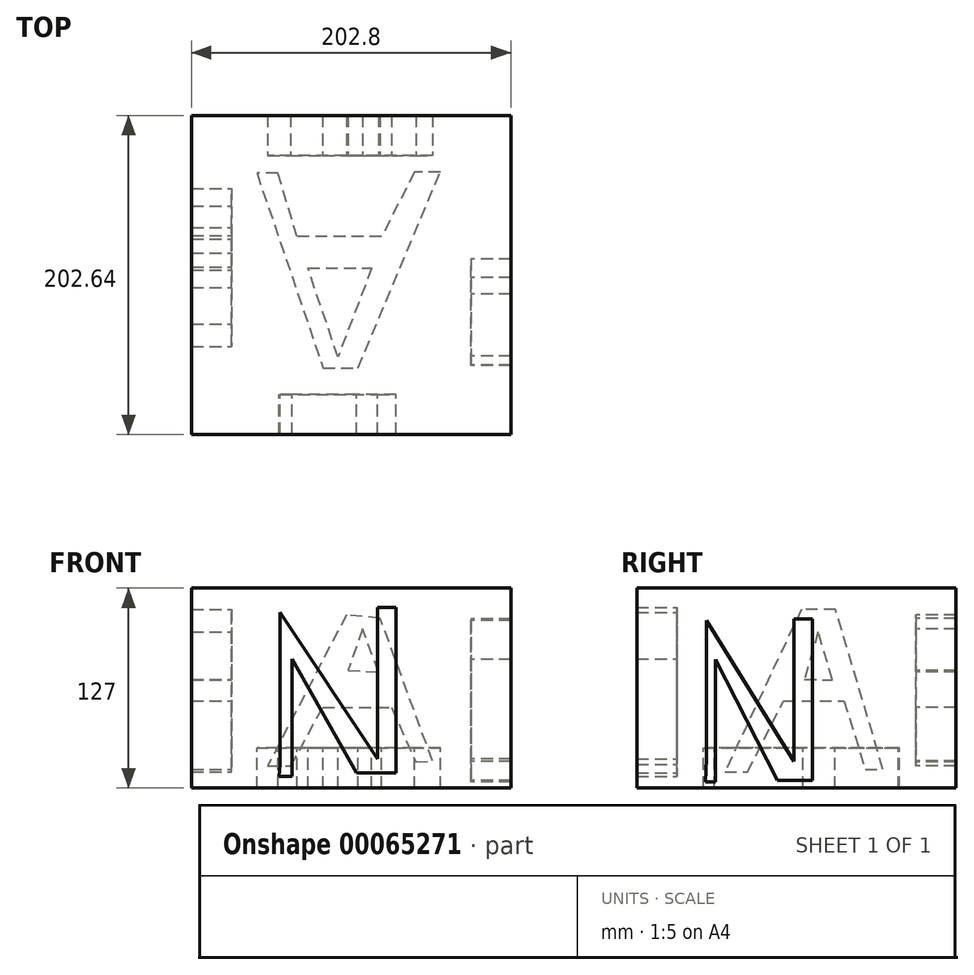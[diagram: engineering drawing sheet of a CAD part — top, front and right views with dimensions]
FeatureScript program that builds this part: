
annotation { "Feature Type Name" : "Feature", "Feature Type Description" : "" }
export const myFeature = defineFeature(function(context is Context, id is Id, definition is map)
    precondition{}
    {
        {
            var Q0;
            Q0=qCreatedBy(makeId("Top.planeOp"),FACE);
            var sketch = newSketch(context, id + "F0", { "sketchPlane" : qUnion([Q0])});
            skLineSegment(sketch, "E0.bottom", {"start": v(-76, 76.16) * mm, "end": v(76, 76.16) * mm});
            skLineSegment(sketch, "E0.top", {"start": v(-76, -75.68) * mm, "end": v(76, -75.68) * mm});
            skLineSegment(sketch, "E0.left", {"start": v(-76, 76.16) * mm, "end": v(-76, -75.68) * mm});
            skLineSegment(sketch, "E0.right", {"start": v(76, 76.16) * mm, "end": v(76, -75.68) * mm});
            skSolve(sketch);
        }
        {
            var Q0;
            Q0=makeQuery(id+"F0.imprint","IMPRINT",FACE,{"disambiguationData":[TD([[makeQuery(id+"F0.imprint","IMPRINT",EDGE,{"derivedFrom":sQuery(id+"F0.wireOp",EDGE,"E0.bottom")}),-1.0]])]});
            extrude(context, id + "F1", {"entities" : qUnion([Q0]), "depth" : 25.4 * mm});
        }
        {
            var Q0;
            Q0=makeQuery(id+"F1.opExtrude","CAP_FACE",FACE,{"disambiguationData":[OSD([sQuery(id+"F0.wireOp",EDGE,"E0.bottom"),sQuery(id+"F0.wireOp",EDGE,"E0.top"),sQuery(id+"F0.wireOp",EDGE,"E0.left"),sQuery(id+"F0.wireOp",EDGE,"E0.right")])],"isStart":false});
            extrude(context, id + "F2", {"entities" : qUnion([Q0]), "operationType" : NewBodyOperationType.ADD, "depth" : 25.4 * mm});
        }
        {
            var Q0;
            Q0=makeQuery(id+"F2.opExtrude","CAP_FACE",FACE,{"disambiguationData":[OSD([sQuery(id+"F0.wireOp",EDGE,"E0.bottom"),sQuery(id+"F0.wireOp",EDGE,"E0.top"),sQuery(id+"F0.wireOp",EDGE,"E0.left"),sQuery(id+"F0.wireOp",EDGE,"E0.right")])],"isStart":false});
            var sketch = newSketch(context, id + "F3", { "sketchPlane" : qUnion([Q0])});
            skLineSegment(sketch, "E1", {"start": v(-54.36, -51.73) * mm, "end": v(-54.36, 43.28) * mm});
            skLineSegment(sketch, "E2", {"start": v(-54.36, 43.28) * mm, "end": v(20.97, -43.16) * mm});
            skLineSegment(sketch, "E3", {"start": v(20.97, -43.16) * mm, "end": v(29.1, -51.72) * mm});
            skLineSegment(sketch, "E4", {"start": v(29.1, -51.72) * mm, "end": v(30.75, 43.95) * mm});
            skLineSegment(sketch, "E5", {"start": v(30.75, 43.95) * mm, "end": v(45.75, 43.7) * mm});
            skLineSegment(sketch, "E6", {"start": v(45.75, 43.7) * mm, "end": v(45.75, -59.02) * mm});
            skLineSegment(sketch, "E7", {"start": v(45.75, -59.02) * mm, "end": v(20.4, -59.02) * mm});
            skLineSegment(sketch, "E8", {"start": v(20.4, -59.02) * mm, "end": v(-46.22, 21.24) * mm});
            skLineSegment(sketch, "E9", {"start": v(-46.22, 21.24) * mm, "end": v(-46.22, -60.24) * mm});
            skLineSegment(sketch, "E10", {"start": v(-46.22, -60.24) * mm, "end": v(-54.78, -60.24) * mm});
            skLineSegment(sketch, "E11", {"start": v(-54.78, -60.24) * mm, "end": v(-54.36, -51.73) * mm});
            skSolve(sketch);
        }
        {
            var Q0;
            Q0=makeQuery(id+"F3.imprint","IMPRINT",FACE,{"disambiguationData":[TD([[makeQuery(id+"F3.imprint","IMPRINT",EDGE,{"derivedFrom":sQuery(id+"F3.wireOp",EDGE,"E1")}),1.0]])]});
            extrude(context, id + "F4", {"entities" : qUnion([Q0]), "operationType" : NewBodyOperationType.ADD, "depth" : 25.4 * mm});
        }
        {
            var Q0;
            Q0=makeQuery(id+"F1.opExtrude","CAP_FACE",FACE,{"disambiguationData":[OSD([sQuery(id+"F0.wireOp",EDGE,"E0.bottom"),sQuery(id+"F0.wireOp",EDGE,"E0.top"),sQuery(id+"F0.wireOp",EDGE,"E0.left"),sQuery(id+"F0.wireOp",EDGE,"E0.right")])],"isStart":true});
            extrude(context, id + "F5", {"entities" : qUnion([Q0]), "operationType" : NewBodyOperationType.ADD, "depth" : 25.4 * mm});
        }
        {
            var Q0;
            Q0=makeQuery(id+"F5.opExtrude","CAP_FACE",FACE,{"disambiguationData":[OSD([sQuery(id+"F0.wireOp",EDGE,"E0.bottom"),sQuery(id+"F0.wireOp",EDGE,"E0.top"),sQuery(id+"F0.wireOp",EDGE,"E0.left"),sQuery(id+"F0.wireOp",EDGE,"E0.right")])],"isStart":false});
            var sketch = newSketch(context, id + "F6", { "sketchPlane" : qUnion([Q0])});
            skLineSegment(sketch, "E12", {"start": v(-59.88, -64.92) * mm, "end": v(-17.83, 58.84) * mm});
            skLineSegment(sketch, "E13", {"start": v(-17.83, 58.84) * mm, "end": v(4.24, 58.84) * mm});
            skLineSegment(sketch, "E14", {"start": v(4.24, 58.84) * mm, "end": v(56.69, -65.72) * mm});
            skLineSegment(sketch, "E15", {"start": v(56.69, -65.72) * mm, "end": v(40.22, -65.72) * mm});
            skLineSegment(sketch, "E16", {"start": v(40.22, -65.72) * mm, "end": v(19.27, -24.63) * mm});
            skLineSegment(sketch, "E17", {"start": v(19.27, -24.63) * mm, "end": v(-34.3, -24.63) * mm});
            skLineSegment(sketch, "E18", {"start": v(-34.3, -24.63) * mm, "end": v(-46.61, -64.92) * mm});
            skLineSegment(sketch, "E19", {"start": v(-46.61, -64.92) * mm, "end": v(-59.88, -64.92) * mm});
            skLineSegment(sketch, "E20", {"start": v(-8.71, 45.41) * mm, "end": v(-28.7, -13.38) * mm});
            skLineSegment(sketch, "E21", {"start": v(-28.7, -13.38) * mm, "end": v(15.91, -13.38) * mm});
            skLineSegment(sketch, "E22", {"start": v(15.91, -13.38) * mm, "end": v(-8.71, 45.41) * mm});
            skSolve(sketch);
        }
        {
            var Q0;
            Q0=makeQuery(id+"F6.imprint","IMPRINT",FACE,{"disambiguationData":[TD([[makeQuery(id+"F6.imprint","IMPRINT",EDGE,{"derivedFrom":sQuery(id+"F6.wireOp",EDGE,"E12")}),1.0]])]});
            extrude(context, id + "F7", {"entities" : qUnion([Q0]), "operationType" : NewBodyOperationType.ADD, "depth" : 25.4 * mm});
        }
        {
            var Q0;
            Q0=makeQuery(id+"F5.opExtrude","CAP_FACE",FACE,{"disambiguationData":[OSD([sQuery(id+"F0.wireOp",EDGE,"E0.bottom"),sQuery(id+"F0.wireOp",EDGE,"E0.top"),sQuery(id+"F0.wireOp",EDGE,"E0.left"),sQuery(id+"F0.wireOp",EDGE,"E0.right")])],"isStart":false});
            var sketch = newSketch(context, id + "F8", { "sketchPlane" : qUnion([Q0])});
            skLineSegment(sketch, "E23", {"start": v(-8.4, 51.8) * mm, "end": v(-27.54, -4.55) * mm});
            skLineSegment(sketch, "E24", {"start": v(-27.54, -4.55) * mm, "end": v(13.03, -4.55) * mm});
            skLineSegment(sketch, "E25", {"start": v(13.03, -4.55) * mm, "end": v(-8.4, 51.8) * mm});
            skSolve(sketch);
        }
        {
            var Q0;
            Q0=makeQuery(id+"F8.imprint","IMPRINT",FACE,{"disambiguationData":[TD([[makeQuery(id+"F8.imprint","IMPRINT",EDGE,{"derivedFrom":sQuery(id+"F8.wireOp",EDGE,"E23")}),1.0]])]});
            extrude(context, id + "F9", {"entities" : qUnion([Q0]), "operationType" : NewBodyOperationType.ADD, "depth" : 25.4 * mm});
        }
        {
            var Q0;
            {var subQ0=sQuery(id+"F0.wireOp",EDGE,"E0.top");Q0=makeQuery(id+"F7.boolean.opBoolean","MERGE",FACE,{"derivedFrom":[makeQuery(id+"F5.boolean.opBoolean","MERGE",FACE,{"derivedFrom":[makeQuery(id+"F4.boolean.opBoolean","MERGE",FACE,{"derivedFrom":[makeQuery(id+"F2.boolean.opBoolean","MERGE",FACE,{"derivedFrom":[makeQuery(id+"F1.opExtrude","SWEPT_FACE",FACE,{"disambiguationData":[OSD([subQ0])]}),makeQuery(id+"F2.opExtrude","SWEPT_FACE",FACE,{"disambiguationData":[OSD([subQ0])]})]}),makeQuery(id+"F4.opExtrude","SWEPT_FACE",FACE,{"disambiguationData":[OSD([subQ0])]})]}),makeQuery(id+"F5.opExtrude","SWEPT_FACE",FACE,{"disambiguationData":[OSD([subQ0])]})]}),makeQuery(id+"F7.opExtrude","SWEPT_FACE",FACE,{"disambiguationData":[OSD([subQ0])]})]});}
            var sketch = newSketch(context, id + "F10", { "sketchPlane" : qUnion([Q0])});
            skLineSegment(sketch, "E26", {"start": v(-45.26, -35.73) * mm, "end": v(-45.26, 60.85) * mm});
            skLineSegment(sketch, "E27", {"start": v(-45.26, 60.85) * mm, "end": v(16.72, -32.28) * mm});
            skLineSegment(sketch, "E28", {"start": v(16.72, -32.28) * mm, "end": v(16.72, 63.93) * mm});
            skLineSegment(sketch, "E29", {"start": v(16.72, 63.93) * mm, "end": v(28.37, 63.93) * mm});
            skLineSegment(sketch, "E30", {"start": v(28.37, 63.93) * mm, "end": v(28.37, -41.2) * mm});
            skLineSegment(sketch, "E31", {"start": v(28.37, -41.2) * mm, "end": v(3.29, -41.2) * mm});
            skLineSegment(sketch, "E32", {"start": v(3.29, -41.2) * mm, "end": v(-37.55, 31.05) * mm});
            skLineSegment(sketch, "E33", {"start": v(-37.55, 31.05) * mm, "end": v(-37.55, -43.29) * mm});
            skLineSegment(sketch, "E34", {"start": v(-37.55, -43.29) * mm, "end": v(-45.73, -43.29) * mm});
            skLineSegment(sketch, "E35", {"start": v(-45.73, -43.29) * mm, "end": v(-45.26, -35.73) * mm});
            skSolve(sketch);
        }
        {
            var Q0;
            Q0=makeQuery(id+"F10.imprint","IMPRINT",FACE,{"disambiguationData":[TD([[makeQuery(id+"F10.imprint","IMPRINT",EDGE,{"derivedFrom":sQuery(id+"F10.wireOp",EDGE,"E26")}),1.0]])]});
            extrude(context, id + "F11", {"entities" : qUnion([Q0]), "operationType" : NewBodyOperationType.ADD, "depth" : 25.4 * mm});
        }
        {
            var Q0;
            {var subQ0=sQuery(id+"F0.wireOp",EDGE,"E0.bottom");Q0=makeQuery(id+"F7.boolean.opBoolean","MERGE",FACE,{"derivedFrom":[makeQuery(id+"F5.boolean.opBoolean","MERGE",FACE,{"derivedFrom":[makeQuery(id+"F4.boolean.opBoolean","MERGE",FACE,{"derivedFrom":[makeQuery(id+"F2.boolean.opBoolean","MERGE",FACE,{"derivedFrom":[makeQuery(id+"F1.opExtrude","SWEPT_FACE",FACE,{"disambiguationData":[OSD([subQ0])]}),makeQuery(id+"F2.opExtrude","SWEPT_FACE",FACE,{"disambiguationData":[OSD([subQ0])]})]}),makeQuery(id+"F4.opExtrude","SWEPT_FACE",FACE,{"disambiguationData":[OSD([subQ0])]})]}),makeQuery(id+"F5.opExtrude","SWEPT_FACE",FACE,{"disambiguationData":[OSD([subQ0])]})]}),makeQuery(id+"F7.opExtrude","SWEPT_FACE",FACE,{"disambiguationData":[OSD([subQ0])]})]});}
            var sketch = newSketch(context, id + "F12", { "sketchPlane" : qUnion([Q0])});
            skLineSegment(sketch, "E36", {"start": v(-51.68, -33.73) * mm, "end": v(-18.36, 56.94) * mm});
            skLineSegment(sketch, "E37", {"start": v(-18.36, 56.94) * mm, "end": v(3.06, 59.07) * mm});
            skLineSegment(sketch, "E38", {"start": v(3.06, 59.07) * mm, "end": v(53.14, -36.86) * mm});
            skLineSegment(sketch, "E39", {"start": v(53.14, -36.86) * mm, "end": v(38.44, -36.86) * mm});
            skLineSegment(sketch, "E40", {"start": v(38.44, -36.86) * mm, "end": v(18.05, 0.39) * mm});
            skLineSegment(sketch, "E41", {"start": v(18.05, 0.39) * mm, "end": v(-25.55, 0.39) * mm});
            skLineSegment(sketch, "E42", {"start": v(-25.55, 0.39) * mm, "end": v(-41, -34.15) * mm});
            skLineSegment(sketch, "E43", {"start": v(-41, -34.15) * mm, "end": v(-51.68, -33.73) * mm});
            skSolve(sketch);
        }
        {
            var Q0;
            Q0=makeQuery(id+"F12.imprint","IMPRINT",FACE,{"disambiguationData":[TD([[makeQuery(id+"F12.imprint","IMPRINT",EDGE,{"derivedFrom":sQuery(id+"F12.wireOp",EDGE,"E36")}),1.0]])]});
            extrude(context, id + "F13", {"entities" : qUnion([Q0]), "operationType" : NewBodyOperationType.ADD, "depth" : 25.4 * mm});
        }
        {
            var Q0;
            {var subQ0=sQuery(id+"F0.wireOp",EDGE,"E0.bottom");Q0=makeQuery(id+"F7.boolean.opBoolean","MERGE",FACE,{"derivedFrom":[makeQuery(id+"F5.boolean.opBoolean","MERGE",FACE,{"derivedFrom":[makeQuery(id+"F4.boolean.opBoolean","MERGE",FACE,{"derivedFrom":[makeQuery(id+"F2.boolean.opBoolean","MERGE",FACE,{"derivedFrom":[makeQuery(id+"F1.opExtrude","SWEPT_FACE",FACE,{"disambiguationData":[OSD([subQ0])]}),makeQuery(id+"F2.opExtrude","SWEPT_FACE",FACE,{"disambiguationData":[OSD([subQ0])]})]}),makeQuery(id+"F4.opExtrude","SWEPT_FACE",FACE,{"disambiguationData":[OSD([subQ0])]})]}),makeQuery(id+"F5.opExtrude","SWEPT_FACE",FACE,{"disambiguationData":[OSD([subQ0])]})]}),makeQuery(id+"F7.opExtrude","SWEPT_FACE",FACE,{"disambiguationData":[OSD([subQ0])]})]});}
            var sketch = newSketch(context, id + "F14", { "sketchPlane" : qUnion([Q0])});
            skLineSegment(sketch, "E44", {"start": v(-17.26, 22.94) * mm, "end": v(-7.29, 50.07) * mm});
            skLineSegment(sketch, "E45", {"start": v(-7.29, 50.07) * mm, "end": v(1.96, 23.8) * mm});
            skLineSegment(sketch, "E46", {"start": v(1.96, 23.8) * mm, "end": v(-17.26, 22.94) * mm});
            skSolve(sketch);
        }
        {
            var Q0;
            Q0=makeQuery(id+"F14.imprint","IMPRINT",FACE,{"disambiguationData":[TD([[makeQuery(id+"F14.imprint","IMPRINT",EDGE,{"derivedFrom":sQuery(id+"F14.wireOp",EDGE,"E44")}),-1.0]])]});
            extrude(context, id + "F15", {"entities" : qUnion([Q0]), "operationType" : NewBodyOperationType.ADD, "depth" : 25.4 * mm});
        }
        {
            var Q0;
            {var subQ0=sQuery(id+"F0.wireOp",EDGE,"E0.right");Q0=makeQuery(id+"F13.boolean.opBoolean","MERGE",FACE,{"derivedFrom":[makeQuery(id+"F11.boolean.opBoolean","MERGE",FACE,{"derivedFrom":[makeQuery(id+"F7.boolean.opBoolean","MERGE",FACE,{"derivedFrom":[makeQuery(id+"F5.boolean.opBoolean","MERGE",FACE,{"derivedFrom":[makeQuery(id+"F4.boolean.opBoolean","MERGE",FACE,{"derivedFrom":[makeQuery(id+"F2.boolean.opBoolean","MERGE",FACE,{"derivedFrom":[makeQuery(id+"F1.opExtrude","SWEPT_FACE",FACE,{"disambiguationData":[OSD([subQ0])]}),makeQuery(id+"F2.opExtrude","SWEPT_FACE",FACE,{"disambiguationData":[OSD([subQ0])]})]}),makeQuery(id+"F4.opExtrude","SWEPT_FACE",FACE,{"disambiguationData":[OSD([subQ0])]})]}),makeQuery(id+"F5.opExtrude","SWEPT_FACE",FACE,{"disambiguationData":[OSD([subQ0])]})]}),makeQuery(id+"F7.opExtrude","SWEPT_FACE",FACE,{"disambiguationData":[OSD([subQ0])]})]}),makeQuery(id+"F11.opExtrude","SWEPT_FACE",FACE,{"disambiguationData":[OSD([sQuery(id+"F0.wireOp",EDGE,"E0.top"),subQ0])]})]}),makeQuery(id+"F13.opExtrude","SWEPT_FACE",FACE,{"disambiguationData":[OSD([sQuery(id+"F0.wireOp",EDGE,"E0.bottom"),subQ0])]})]});}
            var sketch = newSketch(context, id + "F16", { "sketchPlane" : qUnion([Q0])});
            skLineSegment(sketch, "E47", {"start": v(-56.8, -32.44) * mm, "end": v(-56.8, 55.57) * mm});
            skLineSegment(sketch, "E48", {"start": v(-56.8, 55.57) * mm, "end": v(-1.43, -33.78) * mm});
            skLineSegment(sketch, "E49", {"start": v(-1.43, -33.78) * mm, "end": v(-1.43, 56.64) * mm});
            skLineSegment(sketch, "E50", {"start": v(-1.43, 56.64) * mm, "end": v(10.47, 56.64) * mm});
            skLineSegment(sketch, "E51", {"start": v(10.47, 56.64) * mm, "end": v(10.47, 55.97) * mm});
            skLineSegment(sketch, "E52", {"start": v(10.47, 55.97) * mm, "end": v(10.47, -45.82) * mm});
            skLineSegment(sketch, "E53", {"start": v(10.47, -45.82) * mm, "end": v(-11.86, -45.82) * mm});
            skLineSegment(sketch, "E54", {"start": v(-11.86, -45.82) * mm, "end": v(-51.05, 30.82) * mm});
            skLineSegment(sketch, "E55", {"start": v(-51.05, 30.82) * mm, "end": v(-51.05, -46.89) * mm});
            skLineSegment(sketch, "E56", {"start": v(-51.05, -46.89) * mm, "end": v(-57.34, -46.89) * mm});
            skLineSegment(sketch, "E57", {"start": v(-57.34, -46.89) * mm, "end": v(-56.8, -32.44) * mm});
            skSolve(sketch);
        }
        {
            var Q0;
            Q0=makeQuery(id+"F16.imprint","IMPRINT",FACE,{"disambiguationData":[TD([[makeQuery(id+"F16.imprint","IMPRINT",EDGE,{"derivedFrom":sQuery(id+"F16.wireOp",EDGE,"E47")}),1.0]])]});
            extrude(context, id + "F17", {"entities" : qUnion([Q0]), "operationType" : NewBodyOperationType.ADD, "depth" : 25.4 * mm});
        }
        {
            var Q0;
            {var subQ0=sQuery(id+"F0.wireOp",EDGE,"E0.left");Q0=makeQuery(id+"F13.boolean.opBoolean","MERGE",FACE,{"derivedFrom":[makeQuery(id+"F11.boolean.opBoolean","MERGE",FACE,{"derivedFrom":[makeQuery(id+"F7.boolean.opBoolean","MERGE",FACE,{"derivedFrom":[makeQuery(id+"F5.boolean.opBoolean","MERGE",FACE,{"derivedFrom":[makeQuery(id+"F4.boolean.opBoolean","MERGE",FACE,{"derivedFrom":[makeQuery(id+"F2.boolean.opBoolean","MERGE",FACE,{"derivedFrom":[makeQuery(id+"F1.opExtrude","SWEPT_FACE",FACE,{"disambiguationData":[OSD([subQ0])]}),makeQuery(id+"F2.opExtrude","SWEPT_FACE",FACE,{"disambiguationData":[OSD([subQ0])]})]}),makeQuery(id+"F4.opExtrude","SWEPT_FACE",FACE,{"disambiguationData":[OSD([subQ0])]})]}),makeQuery(id+"F5.opExtrude","SWEPT_FACE",FACE,{"disambiguationData":[OSD([subQ0])]})]}),makeQuery(id+"F7.opExtrude","SWEPT_FACE",FACE,{"disambiguationData":[OSD([subQ0])]})]}),makeQuery(id+"F11.opExtrude","SWEPT_FACE",FACE,{"disambiguationData":[OSD([sQuery(id+"F0.wireOp",EDGE,"E0.top"),subQ0])]})]}),makeQuery(id+"F13.opExtrude","SWEPT_FACE",FACE,{"disambiguationData":[OSD([sQuery(id+"F0.wireOp",EDGE,"E0.bottom"),subQ0])]})]});}
            var sketch = newSketch(context, id + "F18", { "sketchPlane" : qUnion([Q0])});
            skLineSegment(sketch, "E58", {"start": v(-55.28, -38.86) * mm, "end": v(-25.19, 62.52) * mm});
            skLineSegment(sketch, "E59", {"start": v(-25.19, 62.52) * mm, "end": v(-3.38, 62.52) * mm});
            skLineSegment(sketch, "E60", {"start": v(-3.38, 62.52) * mm, "end": v(45.17, -40.6) * mm});
            skLineSegment(sketch, "E61", {"start": v(45.17, -40.6) * mm, "end": v(30.72, -40.6) * mm});
            skLineSegment(sketch, "E62", {"start": v(30.72, -40.6) * mm, "end": v(7.85, 4.6) * mm});
            skLineSegment(sketch, "E63", {"start": v(7.85, 4.6) * mm, "end": v(-30.54, 4.6) * mm});
            skLineSegment(sketch, "E64", {"start": v(-30.54, 4.6) * mm, "end": v(-44.04, -38.86) * mm});
            skLineSegment(sketch, "E65", {"start": v(-44.04, -38.86) * mm, "end": v(-55.28, -38.86) * mm});
            skSolve(sketch);
        }
        {
            var Q0;
            Q0=makeQuery(id+"F18.imprint","IMPRINT",FACE,{"disambiguationData":[TD([[makeQuery(id+"F18.imprint","IMPRINT",EDGE,{"derivedFrom":sQuery(id+"F18.wireOp",EDGE,"E58")}),1.0]])]});
            extrude(context, id + "F19", {"entities" : qUnion([Q0]), "operationType" : NewBodyOperationType.ADD, "depth" : 25.4 * mm});
        }
        {
            var Q0;
            {var subQ0=sQuery(id+"F0.wireOp",EDGE,"E0.left");Q0=makeQuery(id+"F13.boolean.opBoolean","MERGE",FACE,{"derivedFrom":[makeQuery(id+"F11.boolean.opBoolean","MERGE",FACE,{"derivedFrom":[makeQuery(id+"F7.boolean.opBoolean","MERGE",FACE,{"derivedFrom":[makeQuery(id+"F5.boolean.opBoolean","MERGE",FACE,{"derivedFrom":[makeQuery(id+"F4.boolean.opBoolean","MERGE",FACE,{"derivedFrom":[makeQuery(id+"F2.boolean.opBoolean","MERGE",FACE,{"derivedFrom":[makeQuery(id+"F1.opExtrude","SWEPT_FACE",FACE,{"disambiguationData":[OSD([subQ0])]}),makeQuery(id+"F2.opExtrude","SWEPT_FACE",FACE,{"disambiguationData":[OSD([subQ0])]})]}),makeQuery(id+"F4.opExtrude","SWEPT_FACE",FACE,{"disambiguationData":[OSD([subQ0])]})]}),makeQuery(id+"F5.opExtrude","SWEPT_FACE",FACE,{"disambiguationData":[OSD([subQ0])]})]}),makeQuery(id+"F7.opExtrude","SWEPT_FACE",FACE,{"disambiguationData":[OSD([subQ0])]})]}),makeQuery(id+"F11.opExtrude","SWEPT_FACE",FACE,{"disambiguationData":[OSD([sQuery(id+"F0.wireOp",EDGE,"E0.top"),subQ0])]})]}),makeQuery(id+"F13.opExtrude","SWEPT_FACE",FACE,{"disambiguationData":[OSD([sQuery(id+"F0.wireOp",EDGE,"E0.bottom"),subQ0])]})]});}
            var sketch = newSketch(context, id + "F20", { "sketchPlane" : qUnion([Q0])});
            skLineSegment(sketch, "E66", {"start": v(-23.11, 17.86) * mm, "end": v(-14.07, 48.34) * mm});
            skLineSegment(sketch, "E67", {"start": v(-14.07, 48.34) * mm, "end": v(-5.4, 18.15) * mm});
            skLineSegment(sketch, "E68", {"start": v(-5.4, 18.15) * mm, "end": v(-23.11, 17.86) * mm});
            skSolve(sketch);
        }
        {
            var Q0;
            Q0=makeQuery(id+"F20.imprint","IMPRINT",FACE,{"disambiguationData":[TD([[makeQuery(id+"F20.imprint","IMPRINT",EDGE,{"derivedFrom":sQuery(id+"F20.wireOp",EDGE,"E66")}),-1.0]])]});
            extrude(context, id + "F21", {"entities" : qUnion([Q0]), "operationType" : NewBodyOperationType.ADD, "depth" : 25.4 * mm});
        }
        {
            var Q0;
            Q0=makeQuery(id+"F2.opExtrude","CAP_FACE",FACE,{"disambiguationData":[OSD([sQuery(id+"F0.wireOp",EDGE,"E0.bottom"),sQuery(id+"F0.wireOp",EDGE,"E0.top"),sQuery(id+"F0.wireOp",EDGE,"E0.left"),sQuery(id+"F0.wireOp",EDGE,"E0.right")])],"isStart":false});
            extrude(context, id + "F22", {"entities" : qUnion([Q0]), "operationType" : NewBodyOperationType.ADD, "depth" : 25.4 * mm});
        }
        {
            var Q0;
            {var subQ0=sQuery(id+"F0.wireOp",EDGE,"E0.right");var subQ1=sQuery(id+"F0.wireOp",EDGE,"E0.left");var subQ2=sQuery(id+"F0.wireOp",EDGE,"E0.top");var subQ3=sQuery(id+"F0.wireOp",EDGE,"E0.bottom");var subQ4=makeQuery(id+"F4.opExtrude","CAP_EDGE",EDGE,{"disambiguationData":[OSD([subQ3])],"isStart":false});var subQ5=makeQuery(id+"F4.opExtrude","CAP_EDGE",EDGE,{"disambiguationData":[OSD([subQ2])],"isStart":false});Q0=makeQuery(id+"F22.boolean.opBoolean","MERGE",FACE,{"derivedFrom":[makeQuery(id+"F19.boolean.opBoolean","MERGE",FACE,{"derivedFrom":[makeQuery(id+"F17.boolean.opBoolean","MERGE",FACE,{"derivedFrom":[makeQuery(id+"F13.boolean.opBoolean","MERGE",FACE,{"derivedFrom":[makeQuery(id+"F11.boolean.opBoolean","MERGE",FACE,{"derivedFrom":[makeQuery(id+"F4.opExtrude","CAP_FACE",FACE,{"disambiguationData":[OSD([subQ3,subQ2,subQ1,subQ0,sQuery(id+"F3.wireOp",EDGE,"E1"),sQuery(id+"F3.wireOp",EDGE,"E2"),sQuery(id+"F3.wireOp",EDGE,"E3"),sQuery(id+"F3.wireOp",EDGE,"E4"),sQuery(id+"F3.wireOp",EDGE,"E5"),sQuery(id+"F3.wireOp",EDGE,"E6"),sQuery(id+"F3.wireOp",EDGE,"E7"),sQuery(id+"F3.wireOp",EDGE,"E8"),sQuery(id+"F3.wireOp",EDGE,"E9"),sQuery(id+"F3.wireOp",EDGE,"E10"),sQuery(id+"F3.wireOp",EDGE,"E11")])],"isStart":false}),makeQuery(id+"F11.opExtrude","SWEPT_FACE",FACE,{"disambiguationData":[OSD([subQ2]),TDD([makeQuery(id+"F10.imprint","IMPRINT",EDGE,{"derivedFrom":subQ5})])]})]}),makeQuery(id+"F13.opExtrude","SWEPT_FACE",FACE,{"disambiguationData":[OSD([subQ3]),TDD([makeQuery(id+"F12.imprint","IMPRINT",EDGE,{"derivedFrom":subQ4})])]})]}),makeQuery(id+"F17.opExtrude","SWEPT_FACE",FACE,{"disambiguationData":[OSD([subQ3,subQ2,subQ0]),TDD([makeQuery(id+"F16.imprint","IMPRINT",EDGE,{"derivedFrom":makeQuery(id+"F13.boolean.opBoolean","MERGE",EDGE,{"derivedFrom":[makeQuery(id+"F11.boolean.opBoolean","MERGE",EDGE,{"derivedFrom":[makeQuery(id+"F4.opExtrude","CAP_EDGE",EDGE,{"disambiguationData":[OSD([subQ0])],"isStart":false}),makeQuery(id+"F11.opExtrude","SWEPT_EDGE",EDGE,{"disambiguationData":[OSD([subQ2,subQ0]),TDD([makeQuery(id+"F10.imprint","INTERSECT",VERTEX,{"derivedFrom":[subQ5,makeQuery(id+"F7.boolean.opBoolean","MERGE",EDGE,{"derivedFrom":[makeQuery(id+"F5.boolean.opBoolean","MERGE",EDGE,{"derivedFrom":[makeQuery(id+"F4.boolean.opBoolean","MERGE",EDGE,{"derivedFrom":[makeQuery(id+"F2.boolean.opBoolean","MERGE",EDGE,{"derivedFrom":[makeQuery(id+"F1.opExtrude","SWEPT_EDGE",EDGE,{"disambiguationData":[OSD([subQ2,subQ0])]}),makeQuery(id+"F2.opExtrude","SWEPT_EDGE",EDGE,{"disambiguationData":[OSD([subQ2,subQ0])]})]}),makeQuery(id+"F4.opExtrude","SWEPT_EDGE",EDGE,{"disambiguationData":[OSD([subQ2,subQ0])]})]}),makeQuery(id+"F5.opExtrude","SWEPT_EDGE",EDGE,{"disambiguationData":[OSD([subQ2,subQ0])]})]}),makeQuery(id+"F7.opExtrude","SWEPT_EDGE",EDGE,{"disambiguationData":[OSD([subQ2,subQ0])]})]})]})])]})]}),makeQuery(id+"F13.opExtrude","SWEPT_EDGE",EDGE,{"disambiguationData":[OSD([subQ3,subQ0]),TDD([makeQuery(id+"F12.imprint","INTERSECT",VERTEX,{"derivedFrom":[subQ4,makeQuery(id+"F7.boolean.opBoolean","MERGE",EDGE,{"derivedFrom":[makeQuery(id+"F5.boolean.opBoolean","MERGE",EDGE,{"derivedFrom":[makeQuery(id+"F4.boolean.opBoolean","MERGE",EDGE,{"derivedFrom":[makeQuery(id+"F2.boolean.opBoolean","MERGE",EDGE,{"derivedFrom":[makeQuery(id+"F1.opExtrude","SWEPT_EDGE",EDGE,{"disambiguationData":[OSD([subQ3,subQ0])]}),makeQuery(id+"F2.opExtrude","SWEPT_EDGE",EDGE,{"disambiguationData":[OSD([subQ3,subQ0])]})]}),makeQuery(id+"F4.opExtrude","SWEPT_EDGE",EDGE,{"disambiguationData":[OSD([subQ3,subQ0])]})]}),makeQuery(id+"F5.opExtrude","SWEPT_EDGE",EDGE,{"disambiguationData":[OSD([subQ3,subQ0])]})]}),makeQuery(id+"F7.opExtrude","SWEPT_EDGE",EDGE,{"disambiguationData":[OSD([subQ3,subQ0])]})]})]})])]})]})})])]})]}),makeQuery(id+"F19.opExtrude","SWEPT_FACE",FACE,{"disambiguationData":[OSD([subQ3,subQ2,subQ1]),TDD([makeQuery(id+"F18.imprint","IMPRINT",EDGE,{"derivedFrom":makeQuery(id+"F13.boolean.opBoolean","MERGE",EDGE,{"derivedFrom":[makeQuery(id+"F11.boolean.opBoolean","MERGE",EDGE,{"derivedFrom":[makeQuery(id+"F4.opExtrude","CAP_EDGE",EDGE,{"disambiguationData":[OSD([subQ1])],"isStart":false}),makeQuery(id+"F11.opExtrude","SWEPT_EDGE",EDGE,{"disambiguationData":[OSD([subQ2,subQ1]),TDD([makeQuery(id+"F10.imprint","INTERSECT",VERTEX,{"derivedFrom":[subQ5,makeQuery(id+"F7.boolean.opBoolean","MERGE",EDGE,{"derivedFrom":[makeQuery(id+"F5.boolean.opBoolean","MERGE",EDGE,{"derivedFrom":[makeQuery(id+"F4.boolean.opBoolean","MERGE",EDGE,{"derivedFrom":[makeQuery(id+"F2.boolean.opBoolean","MERGE",EDGE,{"derivedFrom":[makeQuery(id+"F1.opExtrude","SWEPT_EDGE",EDGE,{"disambiguationData":[OSD([subQ2,subQ1])]}),makeQuery(id+"F2.opExtrude","SWEPT_EDGE",EDGE,{"disambiguationData":[OSD([subQ2,subQ1])]})]}),makeQuery(id+"F4.opExtrude","SWEPT_EDGE",EDGE,{"disambiguationData":[OSD([subQ2,subQ1])]})]}),makeQuery(id+"F5.opExtrude","SWEPT_EDGE",EDGE,{"disambiguationData":[OSD([subQ2,subQ1])]})]}),makeQuery(id+"F7.opExtrude","SWEPT_EDGE",EDGE,{"disambiguationData":[OSD([subQ2,subQ1])]})]})]})])]})]}),makeQuery(id+"F13.opExtrude","SWEPT_EDGE",EDGE,{"disambiguationData":[OSD([subQ3,subQ1]),TDD([makeQuery(id+"F12.imprint","INTERSECT",VERTEX,{"derivedFrom":[subQ4,makeQuery(id+"F7.boolean.opBoolean","MERGE",EDGE,{"derivedFrom":[makeQuery(id+"F5.boolean.opBoolean","MERGE",EDGE,{"derivedFrom":[makeQuery(id+"F4.boolean.opBoolean","MERGE",EDGE,{"derivedFrom":[makeQuery(id+"F2.boolean.opBoolean","MERGE",EDGE,{"derivedFrom":[makeQuery(id+"F1.opExtrude","SWEPT_EDGE",EDGE,{"disambiguationData":[OSD([subQ3,subQ1])]}),makeQuery(id+"F2.opExtrude","SWEPT_EDGE",EDGE,{"disambiguationData":[OSD([subQ3,subQ1])]})]}),makeQuery(id+"F4.opExtrude","SWEPT_EDGE",EDGE,{"disambiguationData":[OSD([subQ3,subQ1])]})]}),makeQuery(id+"F5.opExtrude","SWEPT_EDGE",EDGE,{"disambiguationData":[OSD([subQ3,subQ1])]})]}),makeQuery(id+"F7.opExtrude","SWEPT_EDGE",EDGE,{"disambiguationData":[OSD([subQ3,subQ1])]})]})]})])]})]})})])]})]}),makeQuery(id+"F22.opExtrude","CAP_FACE",FACE,{"disambiguationData":[OSD([subQ3,subQ2,subQ1,subQ0])],"isStart":false})]});}
            var sketch = newSketch(context, id + "F23", { "sketchPlane" : qUnion([Q0])});
            skSolve(sketch);
        }
    });
